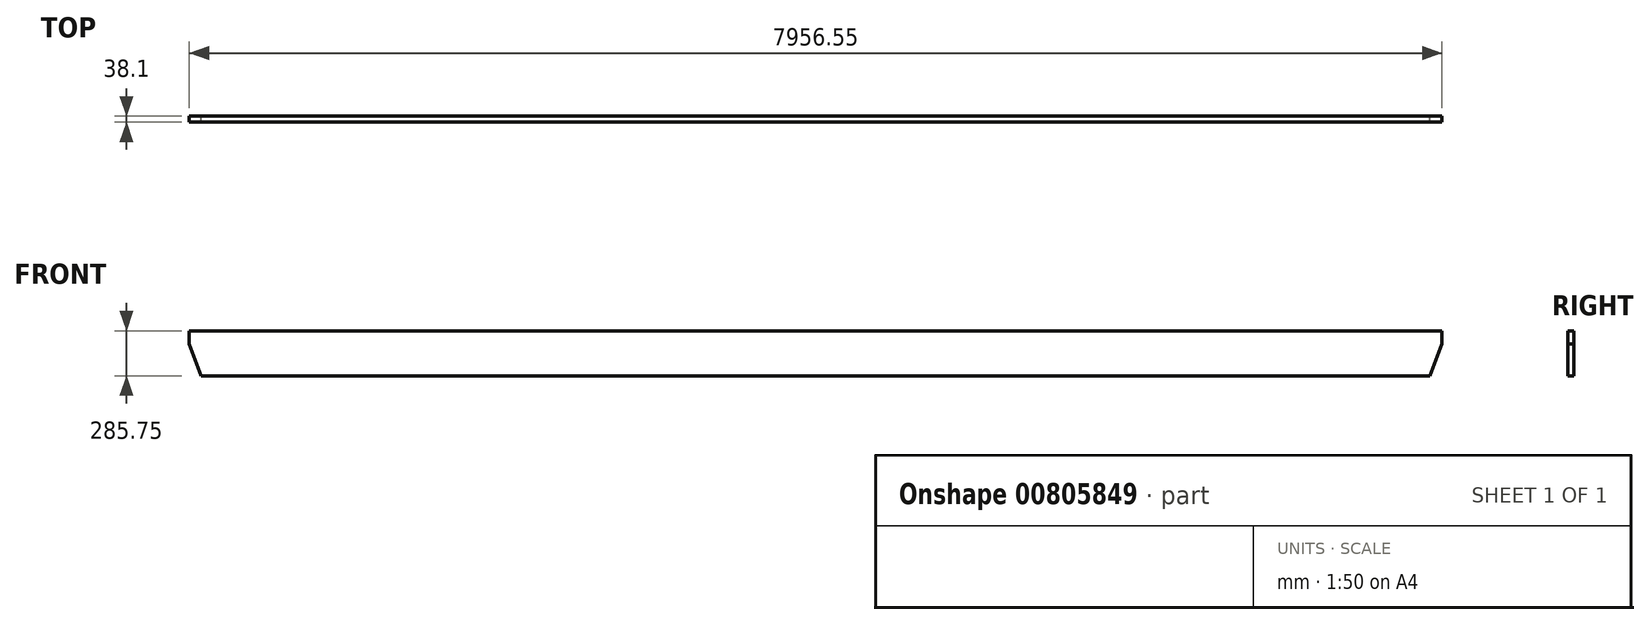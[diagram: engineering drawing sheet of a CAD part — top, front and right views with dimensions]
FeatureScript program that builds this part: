
annotation { "Feature Type Name" : "Feature", "Feature Type Description" : "" }
export const myFeature = defineFeature(function(context is Context, id is Id, definition is map)
    precondition{}
    {
        {
            var Q0;
            Q0=qCreatedBy(makeId("Front.planeOp"),FACE);
            var sketch = newSketch(context, id + "F0", { "sketchPlane" : qUnion([Q0])});
            skLineSegment(sketch, "E0.bottom", {"start": v(0, -309.09) * mm, "end": v(7956.55, -309.09) * mm});
            skLineSegment(sketch, "E0.top", {"start": v(76.2, -594.84) * mm, "end": v(7880.35, -594.84) * mm});
            skLineSegment(sketch, "E0.left", {"start": v(0, -309.09) * mm, "end": v(0, -391.64) * mm});
            skLineSegment(sketch, "E0.right", {"start": v(7956.55, -309.09) * mm, "end": v(7956.55, -391.64) * mm});
            skLineSegment(sketch, "E1", {"start": v(76.2, -594.84) * mm, "end": v(0, -391.64) * mm});
            skLineSegment(sketch, "E2", {"start": v(7880.35, -594.84) * mm, "end": v(7956.55, -391.64) * mm});
            skSolve(sketch);
        }
        {
            var Q0;
            Q0 = qSketchRegion(id + "F0", true);
            extrude(context, id + "F1", {"entities" : qUnion([Q0]), "depth" : 38.1 * mm, "offsetDistance" : 25.4 * mm});
        }
    });
